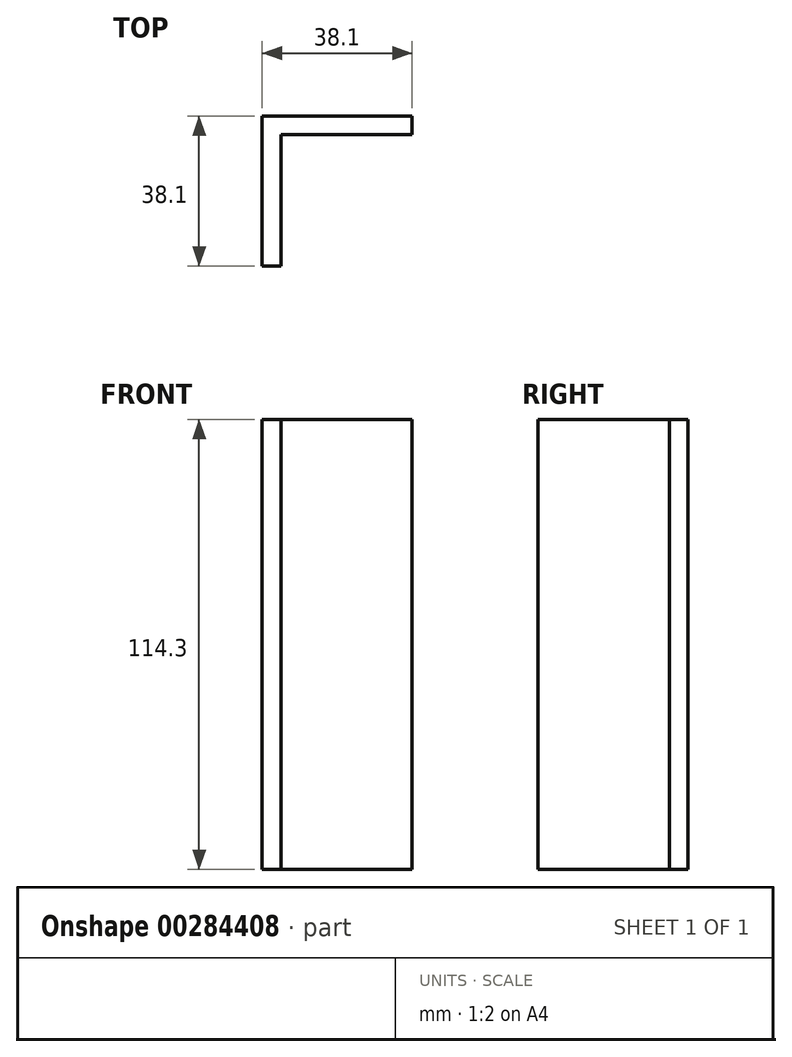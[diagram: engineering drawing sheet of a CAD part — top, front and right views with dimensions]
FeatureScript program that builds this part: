
annotation { "Feature Type Name" : "Feature", "Feature Type Description" : "" }
export const myFeature = defineFeature(function(context is Context, id is Id, definition is map)
    precondition{}
    {
        {
            var Q0;
            Q0=qCreatedBy(makeId("Top.planeOp"),FACE);
            var sketch = newSketch(context, id + "F0", { "sketchPlane" : qUnion([Q0])});
            skLineSegment(sketch, "E0", {"start": v(0, 0) * mm, "end": v(0, -38.1) * mm});
            skLineSegment(sketch, "E1", {"start": v(0, -38.1) * mm, "end": v(4.76, -38.1) * mm});
            skLineSegment(sketch, "E2", {"start": v(4.76, -38.1) * mm, "end": v(4.76, -4.76) * mm});
            skLineSegment(sketch, "E3", {"start": v(4.76, -4.76) * mm, "end": v(38.1, -4.76) * mm});
            skLineSegment(sketch, "E4", {"start": v(38.1, -4.76) * mm, "end": v(38.1, 0) * mm});
            skLineSegment(sketch, "E5", {"start": v(38.1, 0) * mm, "end": v(0, 0) * mm});
            skSolve(sketch);
        }
        {
            var Q0;
            Q0=makeQuery(id+"F0.imprint","IMPRINT",FACE,{"disambiguationData":[TD([[makeQuery(id+"F0.imprint","IMPRINT",EDGE,{"derivedFrom":sQuery(id+"F0.wireOp",EDGE,"E0")}),1.0]])]});
            extrude(context, id + "F1", {"entities" : qUnion([Q0]), "depth" : 114.3 * mm});
        }
    });
